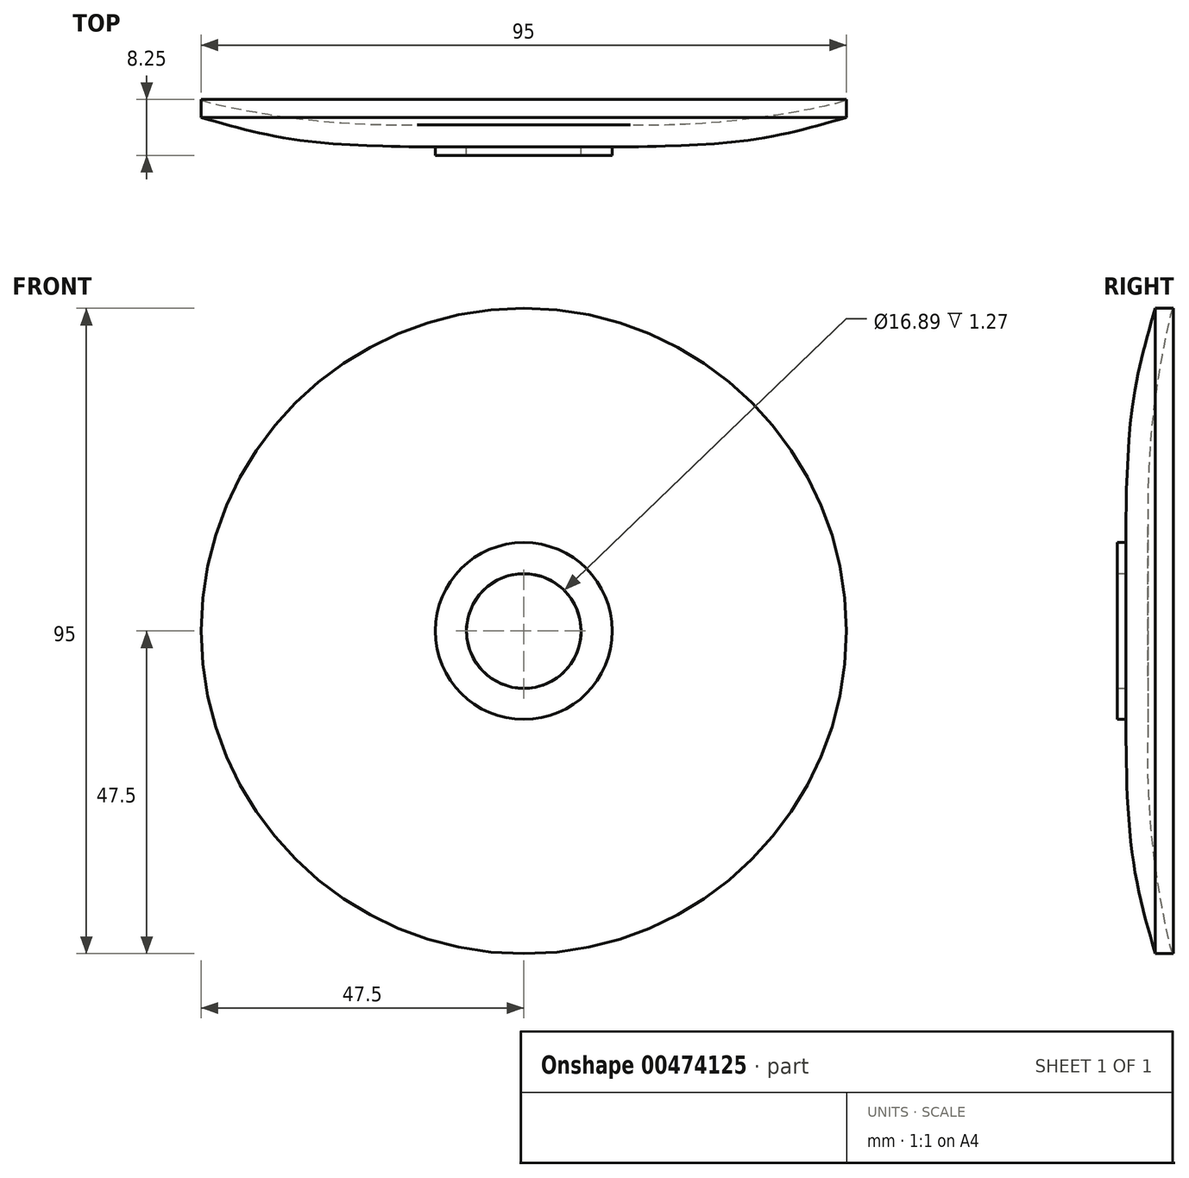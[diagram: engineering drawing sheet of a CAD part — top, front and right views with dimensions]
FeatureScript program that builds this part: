
annotation { "Feature Type Name" : "Feature", "Feature Type Description" : "" }
export const myFeature = defineFeature(function(context is Context, id is Id, definition is map)
    precondition{}
    {
        {
            var Q0;
            Q0=qCreatedBy(makeId("Top.planeOp"),FACE);
            var sketch = newSketch(context, id + "F0", { "sketchPlane" : qUnion([Q0])});
            skLineSegment(sketch, "E0", {"start": v(0, 0) * mm, "end": v(0, 3.23) * mm});
            skFitSpline(sketch, "E1", {"points": [v(0, 3.23) * mm, v(12.04, 3.23) * mm, v(32.47, 4.07) * mm, v(47.49, 6.96) * mm, v(47.49, 7.04) * mm], "startDerivative": vector(40.25, 0.12) * mm, "endDerivative": vector(-1.74, 3.33) * mm});
            skFitSpline(sketch, "E2", {"points": [v(0, 0) * mm, v(12.21, 0) * mm, v(32.73, 0.93) * mm, v(47.5, 4.34) * mm], "startDerivative": vector(38.2, -0.07) * mm, "endDerivative": vector(42.17, 12.25) * mm});
            skLineSegment(sketch, "E3", {"start": v(47.5, 7.02) * mm, "end": v(47.5, 4.34) * mm});
            skSolve(sketch);
        }
        {
            var Q0;
            {var subQ0=sQuery(id+"F0.wireOp",EDGE,"E3");var subQ1=sQuery(id+"F0.wireOp",EDGE,"E1");var subQ2=makeQuery(id+"F0.imprint","INTERSECT",VERTEX,{"disambiguationData":[OD(0.0)],"derivedFrom":[subQ1,subQ0]});Q0=makeQuery(id+"F0.imprint","IMPRINT",FACE,{"disambiguationData":[TD([[makeQuery(id+"F0.imprint","IMPRINT",EDGE,{"disambiguationData":[TD([[subQ2,1.0]])],"derivedFrom":subQ1}),1.0]])]});}
            var Q1;
            {var subQ0=sQuery(id+"F0.wireOp",EDGE,"E0");Q1=makeQuery(id+"F0.imprint","IMPRINT",FACE,{"disambiguationData":[TD([[makeQuery(id+"F0.imprint","IMPRINT",EDGE,{"derivedFrom":subQ0}),-1.0]])]});}
            var Q2;
            Q2=sQuery(id+"F0.wireOp",EDGE,"E0");
            revolve(context, id + "F1", {"entities" : qUnion([Q0, Q1]), "axis" : qUnion([Q2]), "revolveType" : RevolveType.ONE_DIRECTION, "angle" : 360 * degree});
        }
        {
            var Q0;
            Q0=qCreatedBy(makeId("Front.planeOp"),FACE);
            var sketch = newSketch(context, id + "F2", { "sketchPlane" : qUnion([Q0])});
            skCircle(sketch, "E4", {"center": v(0, 0) * mm, "radius": 13.02 * mm});
            skCircle(sketch, "E5", {"center": v(0, 0) * mm, "radius": 8.45 * mm});
            skSolve(sketch);
        }
        {
            var Q0;
            Q0 = qSketchRegion(id + "F2", true);
            extrude(context, id + "F3", {"entities" : qUnion([Q0]), "operationType" : NewBodyOperationType.ADD, "depth" : 1.27 * mm});
        }
    });
